# Revit family: ASL_64_Series_al_door_75mm_jamb_2
name_source: partatom
category: Detail Items
revit_build: Autodesk Revit 2018 (Build: 20170223_1515(x64)
units: mm (PartAtom-declared; Revit-internal decimal feet)

## family parameters
Rotate with component = No
Section Shape = Not Defined
Shared = Yes

## types (5) — shared parameters
Manufacturer = Aluminate Solutions Limited
Technical Info = www.aluminate.nz

## per-type parameters (varying)
| type | ASL_Door_Suite_75mm | ASL_Door_Suite_75mm_Option | Door Depth | Door Stop_50 | Flush Infill | Glazing | Hinge_Single | Type Comments |
| Single Action ASL Hinge Stile Door Suite 75mm | Yes | ASL_Door Suite_Stile_75mm : Hinge Stile Hinge Door 75mm | 46 mm  [stored 0.150919 ft] | Yes | No | No | Yes | ASL 64 Series Jamb 2 With Single Action ASL 75mm Hinge Stile Door Suite |
| Single Action ASL Lockset Stile Door Suite 75mm | Yes | ASL_Door Suite_Stile_75mm : Lockset Stile Hinge Door 75mm | 46 mm  [stored 0.150919 ft] | Yes | No | No | No | ASL 64 Series Jamb 2 With Single Action ASL 75mm Lockset Stile Door Suite |
| Double Action ASL Hinge Stile Door Suite 75mm | Yes | ASL_Door Suite_Stile_75mm : Hinge Stile Hinge Door 75mm | 23 mm | No | Yes | No | No | ASL 64 Series Jamb 2 With Double Action ASL 75mm Hinge Stile Door Suite |
| Glazing | No | ASL_Door Suite_Stile_75mm : Hinge Stile Hinge Door 75mm | 46 mm  [stored 0.150919 ft] | No | No | Yes | No | ASL 64 Series Jamb 2 With Glazing |
| Double Action ASL Lockset Stile Door Suite 75mm | Yes | ASL_Door Suite_Stile_75mm : Lockset Stile Double Action Hinge, Pviot and Sliding Door 75mm | 23 mm | No | Yes | No | No | ASL 64 Series Jamb 2 With Double Action ASL 75mm Lockset Stile Door Suite |

note: [stored X ft] marks values corroborated as IEEE doubles in the binary element streams (Revit-internal decimal feet)

## geometry (parser evidence)
native form markers: Sweep x12
no freeform markers — native parametric forms only
